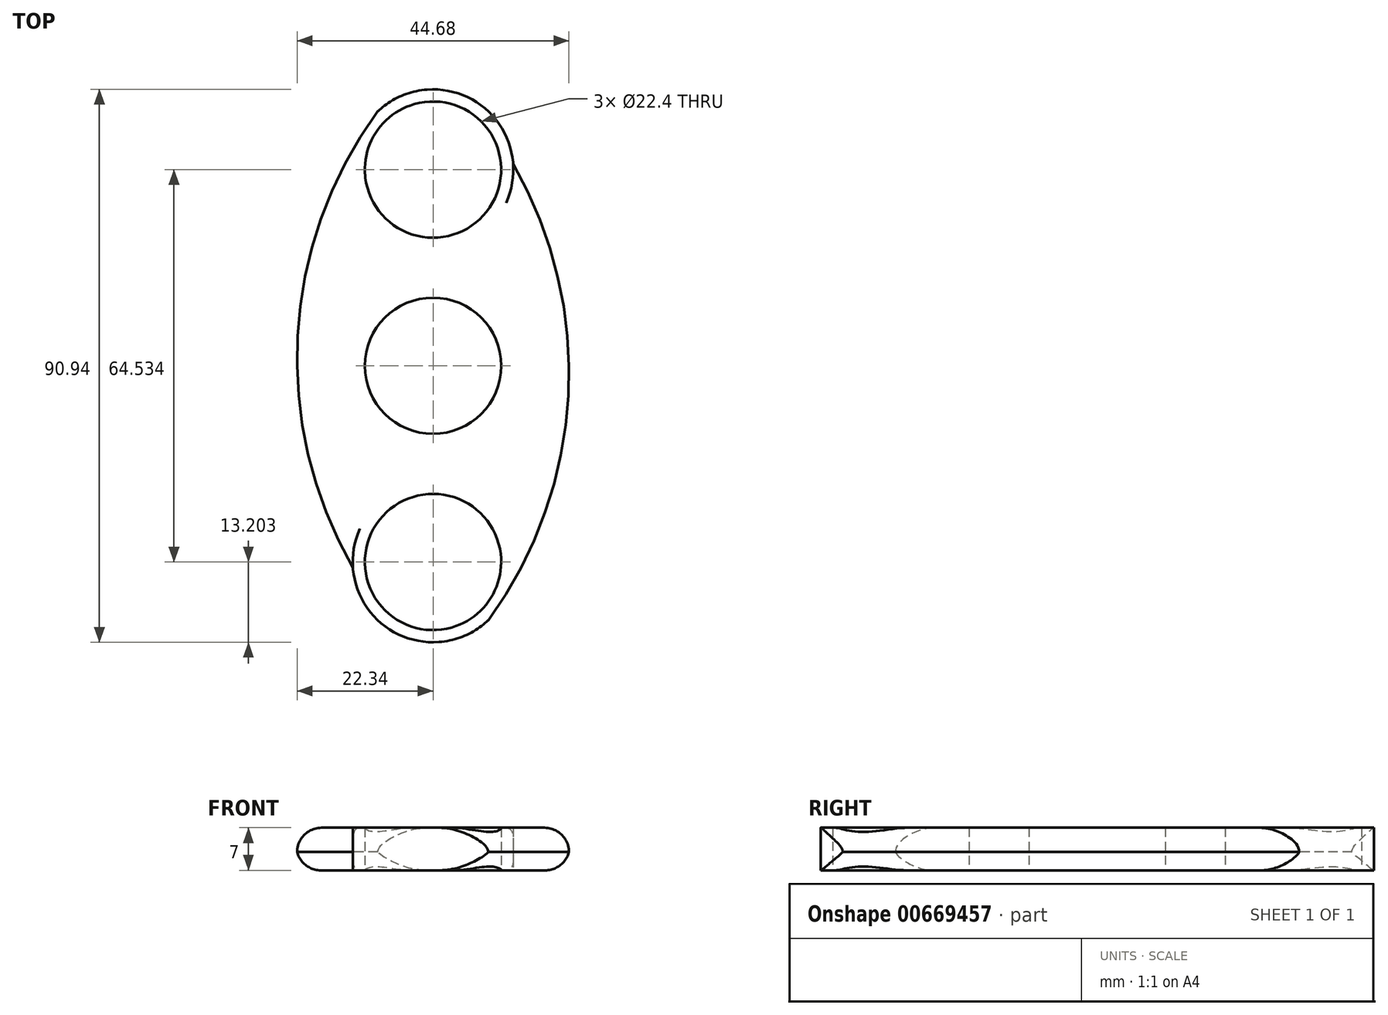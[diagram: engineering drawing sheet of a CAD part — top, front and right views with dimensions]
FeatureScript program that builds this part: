
annotation { "Feature Type Name" : "Feature", "Feature Type Description" : "" }
export const myFeature = defineFeature(function(context is Context, id is Id, definition is map)
    precondition{}
    {
        {
            var Q0;
            Q0=qCreatedBy(makeId("Top.planeOp"),FACE);
            var sketch = newSketch(context, id + "F0", { "sketchPlane" : qUnion([Q0])});
            skCircle(sketch, "E0", {"center": v(0, 0) * mm, "radius": 11.2 * mm});
            skCircle(sketch, "E1", {"center": v(0, 0) * mm, "radius": 13.2 * mm});
            skCircle(sketch, "E2", {"center": v(0, 32.27) * mm, "radius": 11.2 * mm});
            skCircle(sketch, "E3", {"center": v(0, 32.27) * mm, "radius": 13.2 * mm});
            skCircle(sketch, "E4.1.0", {"center": v(0, -32.27) * mm, "radius": 13.2 * mm});
            skCircle(sketch, "E4.1.1", {"center": v(0, -32.27) * mm, "radius": 11.2 * mm});
            skArc(sketch, "E5", {"start": v(-9.1, 41.82) * mm, "mid": v(-22.24, 4.92) * mm, "end": v(-13.17, -33.2) * mm});
            skArc(sketch, "E6.1.0", {"start": v(9.1, -41.82) * mm, "mid": v(22.24, -4.92) * mm, "end": v(13.17, 33.2) * mm});
            skSolve(sketch);
        }
        {
            var Q0;
            Q0=makeQuery(id+"F0.imprint","IMPRINT",FACE,{"disambiguationData":[TD([[makeQuery(id+"F0.imprint","IMPRINT",EDGE,{"derivedFrom":sQuery(id+"F0.wireOp",EDGE,"E1")}),-1.0]])]});
            var Q1;
            Q1=makeQuery(id+"F0.imprint","IMPRINT",FACE,{"disambiguationData":[TD([[makeQuery(id+"F0.imprint","IMPRINT",EDGE,{"derivedFrom":sQuery(id+"F0.wireOp",EDGE,"E0")}),-1.0]])]});
            var Q2;
            Q2=makeQuery(id+"F0.imprint","IMPRINT",FACE,{"disambiguationData":[TD([[makeQuery(id+"F0.imprint","IMPRINT",EDGE,{"derivedFrom":sQuery(id+"F0.wireOp",EDGE,"E2")}),-1.0]])]});
            var Q3;
            Q3=makeQuery(id+"F0.imprint","IMPRINT",FACE,{"disambiguationData":[TD([[makeQuery(id+"F0.imprint","IMPRINT",EDGE,{"derivedFrom":sQuery(id+"F0.wireOp",EDGE,"E4.1.1")}),-1.0]])]});
            extrude(context, id + "F1", {"entities" : qUnion([Q0, Q1, Q2, Q3]), "depth" : 7 * mm, "offsetDistance" : 25 * mm});
        }
        {
            var Q0;
            Q0=makeQuery(id+"F1.opExtrude","CAP_EDGE",EDGE,{"disambiguationData":[OSD([sQuery(id+"F0.wireOp",EDGE,"E6.1.0")])],"isStart":false});
            var Q1;
            Q1=makeQuery(id+"F1.opExtrude","CAP_EDGE",EDGE,{"disambiguationData":[OSD([sQuery(id+"F0.wireOp",EDGE,"E5")])],"isStart":false});
            fillet(context, id + "F2", {"entities" : qUnion([Q0, Q1]), "radius" : 4 * mm, "tangentPropagation" : true, "allowEdgeOverflow" : false});
        }
        {
            var Q0;
            Q0=makeQuery(id+"F1.opExtrude","CAP_EDGE",EDGE,{"disambiguationData":[OSD([sQuery(id+"F0.wireOp",EDGE,"E6.1.0")])],"isStart":true});
            var Q1;
            Q1=makeQuery(id+"F1.opExtrude","CAP_EDGE",EDGE,{"disambiguationData":[OSD([sQuery(id+"F0.wireOp",EDGE,"E5")])],"isStart":true});
            fillet(context, id + "F3", {"entities" : qUnion([Q0, Q1]), "radius" : 4 * mm, "tangentPropagation" : true, "allowEdgeOverflow" : false});
        }
    });
